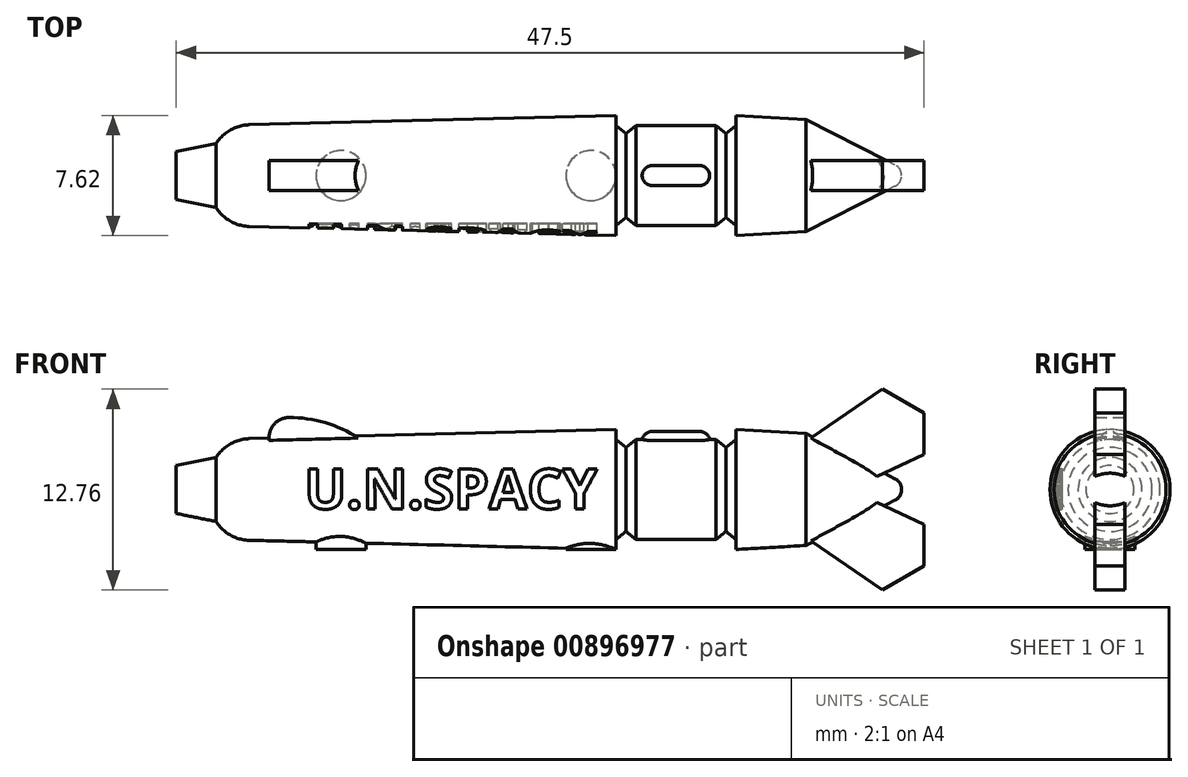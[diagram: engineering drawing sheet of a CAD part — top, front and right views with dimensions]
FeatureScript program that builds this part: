
annotation { "Feature Type Name" : "Feature", "Feature Type Description" : "" }
export const myFeature = defineFeature(function(context is Context, id is Id, definition is map)
    precondition{}
    {
        {
            var Q0;
            Q0=qCreatedBy(makeId("Front.planeOp"),FACE);
            var sketch = newSketch(context, id + "F0", { "sketchPlane" : qUnion([Q0])});
            skLineSegment(sketch, "E0", {"start": v(-36.83, 0) * mm, "end": v(32.69, 0) * mm, "construction": true});
            skLineSegment(sketch, "E1", {"start": v(-27.93, 0) * mm, "end": v(-27.93, 1.52) * mm});
            skLineSegment(sketch, "E2", {"start": v(-27.93, 1.52) * mm, "end": v(-25.4, 2.03) * mm});
            skLineSegment(sketch, "E3", {"start": v(-25.4, 2.03) * mm, "end": v(-25.4, 3.18) * mm});
            skLineSegment(sketch, "E4", {"start": v(-25.4, 3.18) * mm, "end": v(0, 3.81) * mm});
            skLineSegment(sketch, "E5", {"start": v(0, 3.81) * mm, "end": v(0, 3.17) * mm});
            skLineSegment(sketch, "E6", {"start": v(1.27, 3.18) * mm, "end": v(6.35, 3.18) * mm});
            skLineSegment(sketch, "E7", {"start": v(6.99, 2.67) * mm, "end": v(7.62, 3.18) * mm});
            skLineSegment(sketch, "E8", {"start": v(7.62, 3.18) * mm, "end": v(7.62, 3.81) * mm});
            skLineSegment(sketch, "E9", {"start": v(7.62, 3.81) * mm, "end": v(12.07, 3.56) * mm});
            skLineSegment(sketch, "E10", {"start": v(12.07, 3.56) * mm, "end": v(17.73, 0.68) * mm});
            skLineSegment(sketch, "E11", {"start": v(18.14, 0) * mm, "end": v(-27.93, 0) * mm});
            skArc(sketch, "E12", {"start": v(18.14, 0) * mm, "mid": v(18.03, 0.4) * mm, "end": v(17.73, 0.68) * mm});
            skLineSegment(sketch, "E13", {"start": v(6.35, 3.18) * mm, "end": v(6.99, 2.67) * mm});
            skLineSegment(sketch, "E14", {"start": v(3.81, 3.18) * mm, "end": v(3.81, 0) * mm, "construction": true});
            skLineSegment(sketch, "E15.MirrorCS", {"start": v(1.27, 3.18) * mm, "end": v(0.64, 2.67) * mm});
            skLineSegment(sketch, "E16.MirrorCS", {"start": v(0.64, 2.67) * mm, "end": v(0, 3.18) * mm});
            skPoint(sketch, "E17.end.orphan", {"position": v(6.35, 2.16) * mm});
            skPoint(sketch, "E18.orphan", {"position": v(1.27, 2.16) * mm});
            skSolve(sketch);
        }
        {
            var Q0;
            Q0=qSketchRegion(id+"F0",true);
            var Q1;
            Q1=sQuery(id+"F0.wireOp",EDGE,"E11");
            revolve(context, id + "F1", {"entities" : qUnion([Q0]), "axis" : qUnion([Q1]), "revolveType" : RevolveType.FULL});
        }
        {
            var Q0;
            Q0=makeQuery(id+"F1.opRevolve","SWEPT_EDGE",EDGE,{"disambiguationData":[OSD([sQuery(id+"F0.wireOp",EDGE,"E3"),sQuery(id+"F0.wireOp",EDGE,"E4")])]});
            fillet(context, id + "F2", {"entities" : qUnion([Q0]), "radius" : 2.54 * mm, "allowEdgeOverflow" : false});
        }
        {
            var Q0;
            Q0=qCreatedBy(makeId("Front.planeOp"),FACE);
            var sketch = newSketch(context, id + "F3", { "sketchPlane" : qUnion([Q0])});
            skArc(sketch, "E19", {"start": v(-20.77, 4.57) * mm, "mid": v(-22.03, 3.36) * mm, "end": v(-20.88, 2.04) * mm});
            skArc(sketch, "E20", {"start": v(-14.92, 2.04) * mm, "mid": v(-17.58, 3.92) * mm, "end": v(-20.77, 4.57) * mm});
            skLineSegment(sketch, "E21", {"start": v(-20.88, 2.04) * mm, "end": v(-14.92, 2.04) * mm});
            skPoint(sketch, "E22.orphan", {"position": v(12.68, 0) * mm});
            skLineSegment(sketch, "E23", {"start": v(11.6, 2.73) * mm, "end": v(16.93, 6.38) * mm});
            skLineSegment(sketch, "E24", {"start": v(16.93, 6.38) * mm, "end": v(19.57, 4.86) * mm});
            skLineSegment(sketch, "E25", {"start": v(19.57, 4.86) * mm, "end": v(19.57, 2.23) * mm});
            skLineSegment(sketch, "E26", {"start": v(19.57, 2.23) * mm, "end": v(15.53, 0.34) * mm});
            skLineSegment(sketch, "E27", {"start": v(11.6, 2.73) * mm, "end": v(14.4, 0.34) * mm});
            skLineSegment(sketch, "E28", {"start": v(14.8, 0) * mm, "end": v(12.68, 0) * mm, "construction": true});
            skLineSegment(sketch, "E29.MirrorCS", {"start": v(11.6, -2.73) * mm, "end": v(14.4, -0.34) * mm});
            skLineSegment(sketch, "E30.MirrorCS", {"start": v(11.6, -2.73) * mm, "end": v(16.93, -6.38) * mm});
            skLineSegment(sketch, "E31.MirrorCS", {"start": v(19.57, -4.86) * mm, "end": v(19.57, -2.23) * mm});
            skLineSegment(sketch, "E32.MirrorCS", {"start": v(19.57, -2.23) * mm, "end": v(15.53, -0.34) * mm});
            skLineSegment(sketch, "E33", {"start": v(14.4, 0.34) * mm, "end": v(15.53, 0.34) * mm});
            skPoint(sketch, "E34.MirrorCS.end.orphan", {"position": v(19.57, -4.86) * mm});
            skPoint(sketch, "E34.MirrorCS.start.orphan", {"position": v(16.93, -6.38) * mm});
            skLineSegment(sketch, "E35.MirrorCS", {"start": v(14.4, -0.34) * mm, "end": v(15.53, -0.34) * mm});
            skPoint(sketch, "E36.orphan", {"position": v(14.8, 0) * mm});
            skLineSegment(sketch, "E37.MirrorCS", {"start": v(16.93, -6.38) * mm, "end": v(19.57, -4.86) * mm});
            skSolve(sketch);
        }
        {
            var Q0;
            Q0=qSketchRegion(id+"F3",true);
            extrude(context, id + "F4", {"entities" : qUnion([Q0]), "operationType" : NewBodyOperationType.ADD, "endBound" : BoundingType.SYMMETRIC, "depth" : 1.9 * mm, "offsetDistance" : 25.4 * mm});
        }
        {
            var Q0;
            Q0=qCreatedBy(makeId("Front.planeOp"),FACE);
            cPlane(context, id + "F5", {"entities" : qUnion([Q0]), "cplaneType" : CPlaneType.OFFSET, "offset" : 3.05 * mm, "width" : 152.4 * mm, "height" : 152.4 * mm});
        }
        {
            var Q0;
            Q0=qCreatedBy(id+"F5.planeOp",FACE);
            var sketch = newSketch(context, id + "F6", { "sketchPlane" : qUnion([Q0])});
            skText(sketch, "E38", { "text": "U.N.SPACY", "fontName": "OpenSans-Bold.ttf"});
            const initialGuessF6  = {"E38": [-0.01978, -0.00123, 1, 0, 0.00254]};
            skSetInitialGuess(sketch, initialGuessF6);
            skSolve(sketch);
        }
        {
            var Q0;
            Q0=qSketchRegion(id+"F6",true);
            extrude(context, id + "F7", {"entities" : qUnion([Q0]), "operationType" : NewBodyOperationType.REMOVE, "depth" : 25.4 * mm, "offsetDistance" : 25.4 * mm});
        }
        {
            var Q0;
            Q0=qCreatedBy(makeId("Front.planeOp"),FACE);
            var sketch = newSketch(context, id + "F8", { "sketchPlane" : qUnion([Q0])});
            skArc(sketch, "E39", {"start": v(2.29, 3.68) * mm, "mid": v(1.84, 3.5) * mm, "end": v(1.65, 3.05) * mm});
            skLineSegment(sketch, "E40", {"start": v(1.65, 3.05) * mm, "end": v(5.97, 3.05) * mm});
            skLineSegment(sketch, "E41", {"start": v(3.81, 4.43) * mm, "end": v(3.81, -0.67) * mm, "construction": true});
            skArc(sketch, "E42.MirrorC", {"start": v(5.33, 3.68) * mm, "mid": v(5.78, 3.5) * mm, "end": v(5.97, 3.05) * mm});
            skLineSegment(sketch, "E43", {"start": v(2.29, 3.68) * mm, "end": v(5.33, 3.68) * mm});
            skSolve(sketch);
        }
        {
            var Q0;
            Q0=makeQuery(id+"F8.imprint","IMPRINT",FACE,{"disambiguationData":[TD([[makeQuery(id+"F8.imprint","IMPRINT",EDGE,{"derivedFrom":sQuery(id+"F8.wireOp",EDGE,"E39")}),1.0]])]});
            var Q1;
            Q1=sQuery(id+"F8.wireOp",EDGE,"E40");
            revolve(context, id + "F9", {"operationType" : NewBodyOperationType.ADD, "surfaceOperationType" : NewSurfaceOperationType.NEW, "entities" : qUnion([Q0]), "axis" : qUnion([Q1]), "revolveType" : RevolveType.FULL});
        }
        {
            var Q0;
            Q0=qCreatedBy(makeId("Top.planeOp"),FACE);
            cPlane(context, id + "F10", {"entities" : qUnion([Q0]), "cplaneType" : CPlaneType.OFFSET, "offset" : 3.8 * mm, "oppositeDirection" : true, "width" : 152.4 * mm, "height" : 152.4 * mm});
        }
        {
            var Q0;
            Q0=qCreatedBy(id+"F10.planeOp",FACE);
            var sketch = newSketch(context, id + "F11", { "sketchPlane" : qUnion([Q0])});
            skLineSegment(sketch, "E44", {"start": v(0, 0) * mm, "end": v(-43.93, 0) * mm, "construction": true});
            skLineSegment(sketch, "E45", {"start": v(0, 0) * mm, "end": v(0, -1.59) * mm});
            skLineSegment(sketch, "E46", {"start": v(0, -1.59) * mm, "end": v(-3.18, -1.59) * mm});
            skLineSegment(sketch, "E47", {"start": v(-3.18, -1.59) * mm, "end": v(-3.18, 0) * mm});
            skLineSegment(sketch, "E48", {"start": v(-15.88, 0) * mm, "end": v(-15.88, -1.59) * mm});
            skLineSegment(sketch, "E49", {"start": v(-15.88, -1.59) * mm, "end": v(-19.05, -1.59) * mm});
            skLineSegment(sketch, "E50", {"start": v(-19.05, -1.59) * mm, "end": v(-19.05, 0) * mm});
            skLineSegment(sketch, "E51.MirrorCS", {"start": v(-15.88, 0) * mm, "end": v(-15.88, 1.59) * mm});
            skLineSegment(sketch, "E52.MirrorCS", {"start": v(-15.88, 1.59) * mm, "end": v(-19.05, 1.59) * mm});
            skLineSegment(sketch, "E53.MirrorCS", {"start": v(-19.05, 1.59) * mm, "end": v(-19.05, 0) * mm});
            skLineSegment(sketch, "E54.MirrorCS", {"start": v(-3.18, 1.59) * mm, "end": v(-3.18, 0) * mm});
            skLineSegment(sketch, "E55.MirrorCS", {"start": v(0, 1.59) * mm, "end": v(-3.18, 1.59) * mm});
            skLineSegment(sketch, "E56.MirrorCS", {"start": v(0, 0) * mm, "end": v(0, 1.59) * mm});
            skCircle(sketch, "E57", {"center": v(-17.46, 0) * mm, "radius": 0.83 * mm});
            skPoint(sketch, "E57.centerSnap0", {"position": v(-17.46, -1.59) * mm});
            skCircle(sketch, "E58", {"center": v(-1.59, 0) * mm, "radius": 0.83 * mm});
            skPoint(sketch, "E58.centerSnap0", {"position": v(-1.59, -1.59) * mm});
            skSolve(sketch);
        }
        {
            var Q0;
            Q0 = qSketchRegion(id + "F11", true);
            var Q1;
            Q1=makeQuery(id+"F11.imprint","IMPRINT",FACE,{"disambiguationData":[TD([[makeQuery(id+"F11.imprint","IMPRINT",EDGE,{"derivedFrom":sQuery(id+"F11.wireOp",EDGE,"E57")}),1.0]])]});
            var Q2;
            Q2=makeQuery(id+"F11.imprint","IMPRINT",FACE,{"disambiguationData":[TD([[makeQuery(id+"F11.imprint","IMPRINT",EDGE,{"derivedFrom":sQuery(id+"F11.wireOp",EDGE,"E58")}),1.0]])]});
            extrude(context, id + "F12", {"entities" : qUnion([Q0, Q1, Q2]), "operationType" : NewBodyOperationType.ADD, "endBound" : BoundingType.UP_TO_NEXT, "depth" : 25.4 * mm, "offsetDistance" : 25.4 * mm});
        }
        {
            var Q0;
            Q0=makeQuery(id+"F11.imprint","IMPRINT",FACE,{"disambiguationData":[TD([[makeQuery(id+"F11.imprint","IMPRINT",EDGE,{"derivedFrom":sQuery(id+"F11.wireOp",EDGE,"E57")}),1.0]])]});
            var Q1;
            Q1=makeQuery(id+"F11.imprint","IMPRINT",FACE,{"disambiguationData":[TD([[makeQuery(id+"F11.imprint","IMPRINT",EDGE,{"derivedFrom":sQuery(id+"F11.wireOp",EDGE,"E58")}),1.0]])]});
            extrude(context, id + "F13", {"entities" : qUnion([Q0, Q1]), "operationType" : NewBodyOperationType.REMOVE, "oppositeDirection" : true, "depth" : 0.76 * mm, "offsetDistance" : 25.4 * mm});
        }
        {
            var Q0;
            Q0=makeQuery(id+"F12.opExtrude","SWEPT_EDGE",EDGE,{"disambiguationData":[OSD([sQuery(id+"F11.wireOp",EDGE,"E49"),sQuery(id+"F11.wireOp",EDGE,"E50")])]});
            var Q1;
            Q1=makeQuery(id+"F12.opExtrude","SWEPT_EDGE",EDGE,{"disambiguationData":[OSD([sQuery(id+"F11.wireOp",EDGE,"E48"),sQuery(id+"F11.wireOp",EDGE,"E49")])]});
            var Q2;
            Q2=makeQuery(id+"F12.opExtrude","SWEPT_EDGE",EDGE,{"disambiguationData":[OSD([sQuery(id+"F11.wireOp",EDGE,"E51.MirrorCS"),sQuery(id+"F11.wireOp",EDGE,"E52.MirrorCS")])]});
            var Q3;
            Q3=makeQuery(id+"F12.opExtrude","SWEPT_EDGE",EDGE,{"disambiguationData":[OSD([sQuery(id+"F11.wireOp",EDGE,"E52.MirrorCS"),sQuery(id+"F11.wireOp",EDGE,"E53.MirrorCS")])]});
            var Q4;
            Q4=makeQuery(id+"F12.opExtrude","SWEPT_EDGE",EDGE,{"disambiguationData":[OSD([sQuery(id+"F11.wireOp",EDGE,"E54.MirrorCS"),sQuery(id+"F11.wireOp",EDGE,"E55.MirrorCS")])]});
            var Q5;
            Q5=makeQuery(id+"F12.opExtrude","SWEPT_EDGE",EDGE,{"disambiguationData":[OSD([sQuery(id+"F11.wireOp",EDGE,"E46"),sQuery(id+"F11.wireOp",EDGE,"E47")])]});
            var Q6;
            Q6=makeQuery(id+"F12.opExtrude","SWEPT_EDGE",EDGE,{"disambiguationData":[OSD([sQuery(id+"F11.wireOp",EDGE,"E55.MirrorCS"),sQuery(id+"F11.wireOp",EDGE,"E56.MirrorCS")])]});
            var Q7;
            Q7=makeQuery(id+"F12.opExtrude","SWEPT_EDGE",EDGE,{"disambiguationData":[OSD([sQuery(id+"F11.wireOp",EDGE,"E45"),sQuery(id+"F11.wireOp",EDGE,"E46")])]});
            fillet(context, id + "F14", {"entities" : qUnion([Q0, Q1, Q2, Q3, Q4, Q5, Q6, Q7]), "radius" : 1.59 * mm, "tangentPropagation" : true, "allowEdgeOverflow" : false});
        }
    });
